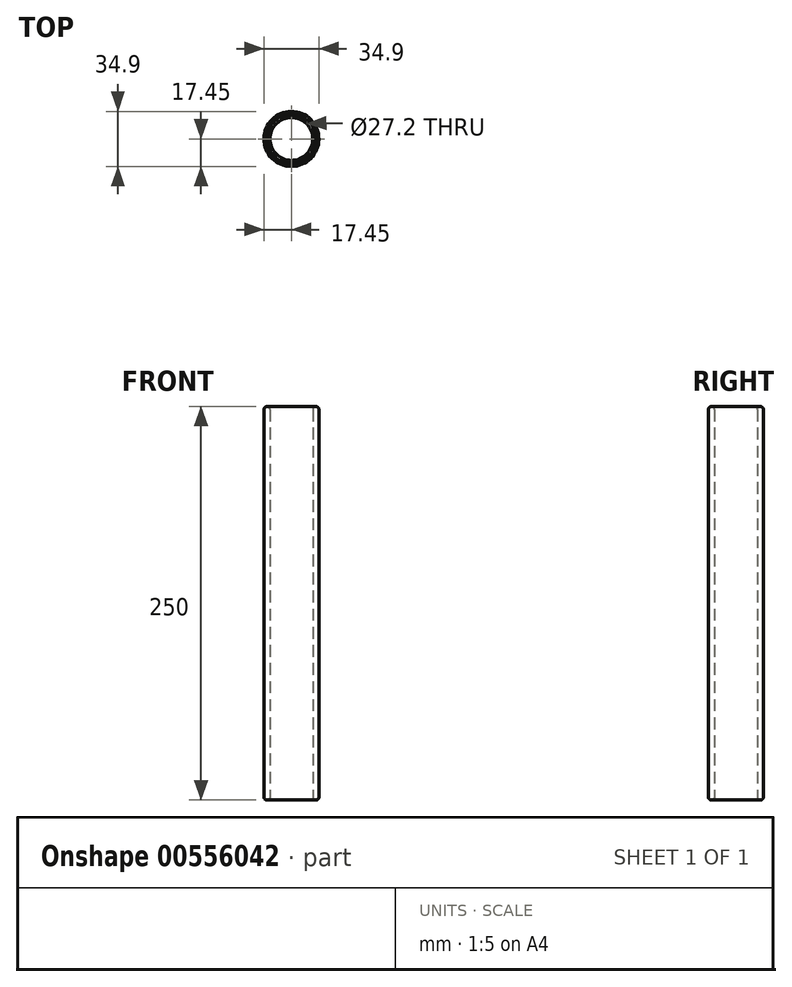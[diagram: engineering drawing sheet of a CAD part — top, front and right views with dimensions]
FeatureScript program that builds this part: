
annotation { "Feature Type Name" : "Feature", "Feature Type Description" : "" }
export const myFeature = defineFeature(function(context is Context, id is Id, definition is map)
    precondition{}
    {
        {
            var Q0;
            Q0=qCreatedBy(makeId("Top.planeOp"),FACE);
            var sketch = newSketch(context, id + "F0", { "sketchPlane" : qUnion([Q0])});
            skCircle(sketch, "E0", {"center": v(0, 0) * mm, "radius": 17.45 * mm});
            skCircle(sketch, "E1", {"center": v(0, 0) * mm, "radius": 13.6 * mm});
            skSolve(sketch);
        }
        {
            var Q0;
            Q0=makeQuery(id+"F0.imprint","IMPRINT",FACE,{"disambiguationData":[TD([[makeQuery(id+"F0.imprint","IMPRINT",EDGE,{"derivedFrom":sQuery(id+"F0.wireOp",EDGE,"E0")}),1.0]])]});
            extrude(context, id + "F1", {"entities" : qUnion([Q0]), "depth" : 250 * mm, "offsetDistance" : 25 * mm});
        }
        {
            var Q0;
            Q0=makeQuery(id+"F1.opExtrude","CAP_EDGE",EDGE,{"disambiguationData":[OSD([sQuery(id+"F0.wireOp",EDGE,"E1")])],"isStart":false});
            fillet(context, id + "F2", {"entities" : qUnion([Q0]), "radius" : 2 * mm, "tangentPropagation" : true, "allowEdgeOverflow" : false});
        }
        {
            var Q0;
            Q0=makeQuery(id+"F1.opExtrude","CAP_EDGE",EDGE,{"disambiguationData":[OSD([sQuery(id+"F0.wireOp",EDGE,"E0")])],"isStart":false});
            fillet(context, id + "F3", {"entities" : qUnion([Q0]), "radius" : 2 * mm, "tangentPropagation" : true, "allowEdgeOverflow" : false});
        }
        {
            var Q0;
            Q0=makeQuery(id+"F1.opExtrude","CAP_EDGE",EDGE,{"disambiguationData":[OSD([sQuery(id+"F0.wireOp",EDGE,"E1")])],"isStart":true});
            fillet(context, id + "F4", {"entities" : qUnion([Q0]), "radius" : 2 * mm, "tangentPropagation" : true, "allowEdgeOverflow" : false});
        }
        {
            var Q0;
            Q0=makeQuery(id+"F1.opExtrude","CAP_EDGE",EDGE,{"disambiguationData":[OSD([sQuery(id+"F0.wireOp",EDGE,"E0")])],"isStart":true});
            fillet(context, id + "F5", {"entities" : qUnion([Q0]), "radius" : 2 * mm, "tangentPropagation" : true, "allowEdgeOverflow" : false});
        }
    });
